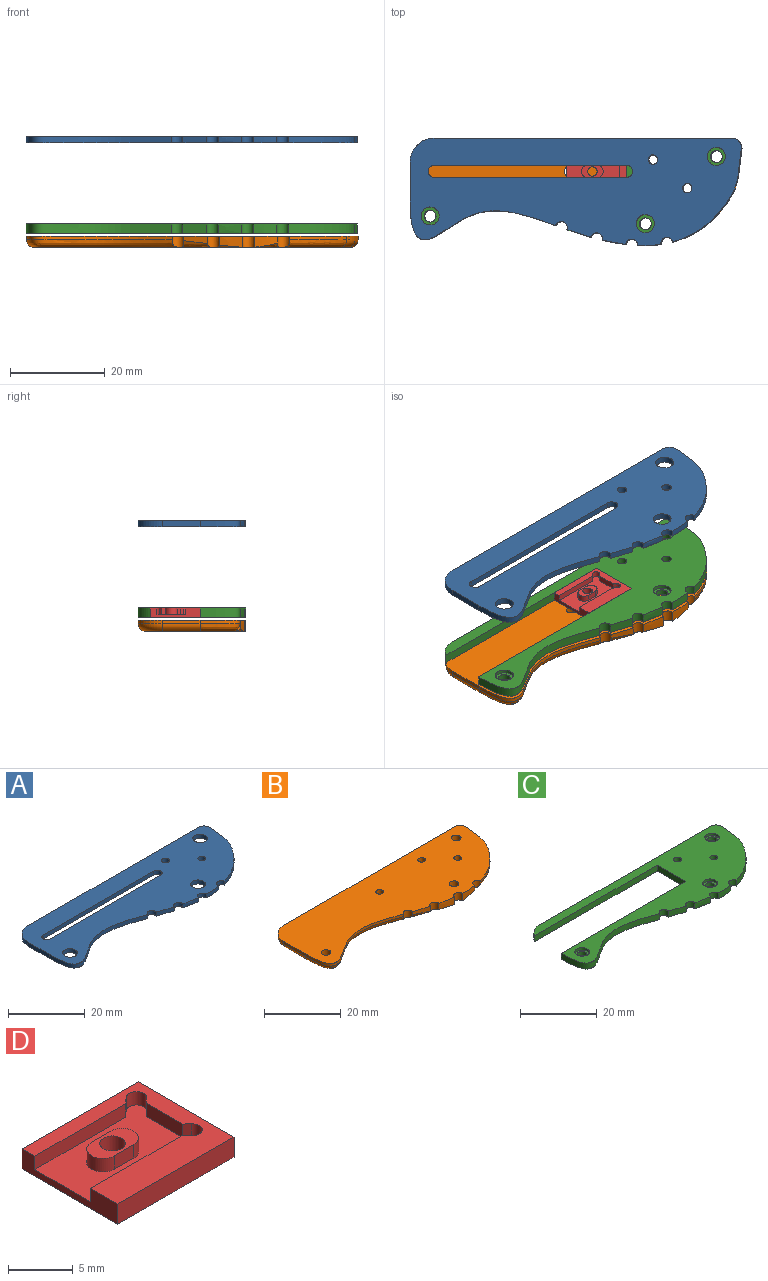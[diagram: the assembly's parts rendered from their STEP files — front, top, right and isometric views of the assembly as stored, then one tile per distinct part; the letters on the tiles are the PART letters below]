
ASSEMBLY  parts=4 mates=3
PART A: 26 faces, bbox 69.9x23.5x1.3 mm
  f0: plane 69.91x23.5mm, normal (0,0,-1), area 1147mm2, adj f2,f3,f4,f5,f6,f7,f8,f9
  f1: plane 69.91x23.5mm, normal (0,0,1), area 1147mm2, adj f2,f3,f4,f5,f6,f7,f8,f9
  f2: cylinder r=5.08mm len=5.08mm, axis (0,0,-1), area 10.1mm2, adj f0,f1,f3,f15
  f3: plane 62.8x1.27mm, normal (0,1,0), area 79.8mm2, adj f0,f1,f2,f4
  f4: cylinder r=2.03mm len=2.28mm, axis (0,0,-1), area 4.4mm2, adj f0,f1,f3,f5
  f5: plane 5.5x1.27mm, normal (0.99,-0.12,0), area 7mm2, adj f0,f1,f4,f6
  f6: cylinder r=11.43mm len=4.75mm, axis (0,0,-1), area 6.5mm2, adj f0,f1,f5,f7
  f7: extruded ~12.06x9.35mm, area 19.8mm2, adj f0,f1,f6,f8
  f8: cylinder r=1.27mm len=2.5mm, axis (0,0,-1), area 5mm2, adj f0,f1,f7,f9
  f9: extruded ~4.92x1.27mm, area 6.3mm2, adj f0,f1,f8,f10
  f10: cylinder r=1.27mm len=2.53mm, axis (0,0,-1), area 5mm2, adj f0,f1,f9,f11
  f11: extruded ~4.94x1.27mm, area 6.4mm2, adj f0,f1,f10,f12
  f12: cylinder r=1.27mm len=2.5mm, axis (0,0,-1), area 5mm2, adj f0,f1,f11,f13
  f13: extruded ~5.01x1.6mm, area 6.7mm2, adj f0,f1,f12,f14
  f14: cylinder r=1.27mm len=2.47mm, axis (0,0,-1), area 5.1mm2, adj f0,f1,f13,f16
  f15: plane 7.94x1.27mm, normal (-1,0,0), area 10.1mm2, adj f0,f1,f2,f16
  f16: extruded ~30.72x8.36mm, area 49.9mm2, adj f0,f1,f14,f15
  f17: cylinder r=1.27mm len=2.54mm, axis (0,0,1), area 5.1mm2, adj f0,f1,f18,f20
  f18: plane 40.64x1.27mm, normal (0,-1,0), area 51.6mm2, adj f0,f1,f17,f19
  f19: cylinder r=1.27mm len=2.54mm, axis (0,0,1), area 5.1mm2, adj f0,f1,f18,f20
  f20: plane 40.64x1.27mm, normal (0,1,0), area 51.6mm2, adj f0,f1,f17,f19
  f21: cylinder r=1mm len=2mm, axis (0,0,-1), area 8mm2, adj f0,f1
  f22: cylinder r=1mm len=2mm, axis (0,0,-1), area 8mm2, adj f0,f1
  f23: cylinder r=1.9mm len=3.8mm, axis (0,0,1), area 15.2mm2, adj f0,f1
  f24: cylinder r=1.9mm len=3.8mm, axis (0,0,1), area 15.2mm2, adj f0,f1
  f25: cylinder r=1.9mm len=3.8mm, axis (0,0,1), area 15.2mm2, adj f0,f1
PART B: 38 faces, bbox 71.2x31x2.4 mm
  f0: plane 66.74x20.69mm, normal (0,0,-1), area 899mm2, adj f11,f17,f18,f19,f20,f21,f22,f23
  f1: plane 69.91x23.5mm, normal (0,0,1), area 1271.4mm2, adj f2,f3,f4,f5,f6,f7,f8,f9
  f2: plane 7.94x0.79mm, normal (-1,0,0), area 6.3mm2, adj f1,f3,f16,f31
  f3: cylinder r=5.08mm len=5.08mm, axis (0,0,1), area 6.3mm2, adj f1,f2,f4,f32
  f4: plane 62.8x0.79mm, normal (0,1,0), area 49.8mm2, adj f1,f3,f5,f33
  f5: cylinder r=2.03mm len=2.28mm, axis (0,0,1), area 2.7mm2, adj f1,f4,f6,f34
  f6: plane 5.5x0.79mm, normal (0.99,-0.12,0), area 4.4mm2, adj f1,f5,f7,f35
  f7: cylinder r=11.43mm len=4.75mm, axis (0,0,1), area 4mm2, adj f1,f6,f8,f36
  f8: extruded ~12.06x9.35mm, area 12.4mm2, adj f1,f7,f9,f37
  f9: cylinder r=1.27mm len=2.5mm, axis (0,0,1), area 8.3mm2, adj f1,f8,f10,f37
  f10: extruded ~4.92x2.34mm, area 9.4mm2, adj f1,f9,f11,f37
  f11: cylinder r=1.27mm len=2.53mm, axis (0,0,1), area 9.4mm2, adj f0,f1,f10,f12,f30,f37
  f12: extruded ~4.94x2.34mm, area 10.6mm2, adj f1,f11,f13,f30
  f13: cylinder r=1.27mm len=2.5mm, axis (0,0,1), area 6.8mm2, adj f1,f12,f14,f30
  f14: extruded ~5.01x1.6mm, area 6.6mm2, adj f1,f13,f15,f30
  f15: cylinder r=1.27mm len=2.47mm, axis (0,0,1), area 8.3mm2, adj f1,f14,f16,f30
  f16: extruded ~30.72x8.36mm, area 31.2mm2, adj f1,f2,f15,f30
  f17: cylinder r=1.25mm len=2.5mm, axis (0,0,1), area 18.7mm2, adj f0,f1
  f18: cylinder r=1.25mm len=2.5mm, axis (0,0,1), area 18.7mm2, adj f0,f1
  f19: cylinder r=1.25mm len=2.5mm, axis (0,0,1), area 18.7mm2, adj f0,f1
  f20: cylinder r=1mm len=2.38mm, axis (0,0,1), area 15mm2, adj f0,f1
  f21: plane 11.32x0.79mm, normal (0,1,0), area 9mm2, adj f0,f22,f26,f27
  f22: cylinder r=1.27mm len=1.27mm, axis (0,0,-1), area 1.6mm2, adj f0,f21,f23,f27
  f23: plane 7.94x0.79mm, normal (1,0,0), area 6.3mm2, adj f0,f22,f24,f27
  f24: cylinder r=1.27mm len=1.27mm, axis (0,0,-1), area 1.6mm2, adj f0,f23,f25,f27
  f25: plane 11.32x0.79mm, normal (0,-1,0), area 9mm2, adj f0,f24,f26,f27
  f26: plane 10.48x0.79mm, normal (-1,0,0), area 8.3mm2, adj f0,f21,f25,f27
  f27: plane 12.59x10.48mm, normal (0,0,-1), area 124.9mm2, adj f21,f22,f23,f24,f25,f26,f28,f29
  f28: cylinder r=1mm len=2mm, axis (0,0,-1), area 10mm2, adj f1,f27
  f29: cylinder r=1mm len=2mm, axis (0,0,-1), area 10mm2, adj f1,f27
  f30: bspline ~65.23x24.38mm, area 114.3mm2, adj f0,f11,f12,f13,f14,f15,f16,f31
  f31: cylinder r=1.59mm len=7.94mm, axis (0,-1,0), area 19.8mm2, adj f0,f2,f30,f32
  f32: torus R=3.49mm, axis (0,0,-1), area 17.6mm2, adj f0,f3,f31,f33
  f33: cylinder r=1.59mm len=62.8mm, axis (-1,0,0), area 156.6mm2, adj f0,f4,f32,f34
  f34: torus R=0.45mm, axis (0,0,-1), area 6.2mm2, adj f0,f5,f33,f35
  f35: cylinder r=1.59mm len=5.69mm, axis (0.12,0.99,0), area 13.8mm2, adj f0,f6,f34,f36
  f36: torus R=9.84mm, axis (0,0,-1), area 12.1mm2, adj f0,f7,f35,f37
  f37: bspline ~30.16x19.22mm, area 44.5mm2, adj f0,f8,f9,f10,f11,f36
PART C: 30 faces, bbox 69.9x23.5x1.9 mm
  f0: cylinder r=1.25mm len=2.5mm, axis (0,0,1), area 9.2mm2, adj f21,f26
  f1: cylinder r=1.25mm len=2.5mm, axis (0,0,1), area 9.2mm2, adj f21,f24
  f2: cylinder r=1.25mm len=2.5mm, axis (0,0,1), area 9.2mm2, adj f21,f28
  f3: plane 69.91x23.5mm, normal (0,0,1), area 776.8mm2, adj f4,f5,f6,f7,f8,f9,f10,f11
  f4: plane 45.04x1.91mm, normal (0,-1,0), area 85.8mm2, adj f3,f5,f20,f21
  f5: plane 10.48x1.91mm, normal (-1,0,0), area 20mm2, adj f3,f4,f6,f21
  f6: plane 45.72x1.91mm, normal (0,1,0), area 87.1mm2, adj f3,f5,f7,f21
  f7: extruded ~30.72x8.36mm, area 74.8mm2, adj f3,f6,f8,f21
  f8: cylinder r=1.27mm len=2.47mm, axis (0,0,1), area 7.6mm2, adj f3,f7,f9,f21
  f9: extruded ~5.01x1.91mm, area 10mm2, adj f3,f8,f10,f21
  f10: cylinder r=1.27mm len=2.5mm, axis (0,0,1), area 7.5mm2, adj f3,f9,f11,f21
  f11: extruded ~4.94x1.91mm, area 9.6mm2, adj f3,f10,f12,f21
  f12: cylinder r=1.27mm len=2.53mm, axis (0,0,1), area 7.5mm2, adj f3,f11,f13,f21
  f13: extruded ~4.92x1.91mm, area 9.4mm2, adj f3,f12,f14,f21
  f14: cylinder r=1.27mm len=2.5mm, axis (0,0,1), area 7.5mm2, adj f3,f13,f15,f21
  f15: extruded ~12.06x9.35mm, area 29.8mm2, adj f3,f14,f16,f21
  f16: cylinder r=11.43mm len=4.75mm, axis (0,0,1), area 9.7mm2, adj f3,f15,f17,f21
  f17: plane 5.5x1.91mm, normal (0.99,-0.12,0), area 10.5mm2, adj f3,f16,f18,f21
  f18: cylinder r=2.03mm len=2.28mm, axis (0,0,1), area 6.6mm2, adj f3,f17,f19,f21
  f19: plane 62.8x1.91mm, normal (0,1,0), area 119.6mm2, adj f3,f18,f20,f21
  f20: cylinder r=5.08mm len=4.4mm, axis (0,0,1), area 10.1mm2, adj f3,f4,f19,f21
  f21: plane 69.91x23.5mm, normal (0,0,-1), area 796.1mm2, adj f0,f1,f2,f4,f5,f6,f7,f8
  f22: cylinder r=1mm len=2mm, axis (0,0,-1), area 12mm2, adj f3,f21
  f23: cylinder r=1mm len=2mm, axis (0,0,-1), area 12mm2, adj f3,f21
  f24: plane 3.8x3.8mm, normal (0,0,1), area 6.4mm2, adj f1,f25
  f25: cylinder r=1.9mm len=3.8mm, axis (0,0,1), area 8.7mm2, adj f3,f24
  f26: plane 3.8x3.8mm, normal (0,0,1), area 6.4mm2, adj f0,f27
  f27: cylinder r=1.9mm len=3.8mm, axis (0,0,1), area 8.7mm2, adj f3,f26
  f28: plane 3.8x3.8mm, normal (0,0,1), area 6.4mm2, adj f2,f29
  f29: cylinder r=1.9mm len=3.8mm, axis (0,0,1), area 8.7mm2, adj f3,f28
PART D: 24 faces, bbox 12.7x10.5x1.9 mm
  f0: plane 3.98x1.27mm, normal (-1,0,0), area 5.1mm2, adj f1,f2,f16,f21
  f1: plane 12.7x10.48mm, normal (0,0,1), area 62.1mm2, adj f0,f3,f4,f5,f6,f7,f14,f15
  f2: plane 11.91x7.68mm, normal (0,0,1), area 60.6mm2, adj f0,f5,f6,f7,f8,f9,f12,f13
  f3: plane 10.48x1.91mm, normal (1,0,0), area 20mm2, adj f1,f4,f22,f23
  f4: plane 12.7x1.91mm, normal (0,1,0), area 24.2mm2, adj f1,f3,f5,f23
  f5: plane 10.48x1.91mm, normal (-1,0,0), area 12.2mm2, adj f1,f2,f4,f6,f7,f22,f23
  f6: plane 9.92x1.27mm, normal (0,-1,0), area 12.6mm2, adj f1,f2,f5,f15
  f7: plane 9.92x1.27mm, normal (0,1,0), area 12.6mm2, adj f1,f2,f5,f18
  f8: plane 2.1x1.27mm, normal (0,-1,0), area 2.7mm2, adj f2,f9,f10,f12
  f9: cylinder r=1.27mm len=2.54mm, axis (0,0,1), area 5.1mm2, adj f2,f8,f10,f13
  f10: plane 4.64x2.54mm, normal (0,0,1), area 7.2mm2, adj f8,f9,f11,f12,f13
  f11: cylinder r=1mm len=2mm, axis (0,0,1), area 12mm2, adj f10,f23
  f12: cylinder r=1.27mm len=2.54mm, axis (0,0,1), area 5.1mm2, adj f2,f8,f10,f13
  f13: plane 2.1x1.27mm, normal (0,1,0), area 2.7mm2, adj f2,f9,f10,f12
  f14: plane 1.27x0.6mm, normal (0.66,-0.75,0), area 1mm2, adj f1,f2,f15,f17
  f15: cylinder r=0.79mm len=1.27mm, axis (0,0,1), area 0.1mm2, adj f1,f2,f6,f14
  f16: plane 1.27x0.52mm, normal (-0.66,0.75,0), area 0.9mm2, adj f0,f1,f2,f17
  f17: cylinder r=0.79mm len=1.39mm, axis (0,0,1), area 3.2mm2, adj f1,f2,f14,f16
  f18: cylinder r=0.79mm len=1.27mm, axis (0,0,1), area 0.1mm2, adj f1,f2,f7,f19
  f19: plane 1.27x0.6mm, normal (0.66,0.75,0), area 1mm2, adj f1,f2,f18,f20
  f20: cylinder r=0.79mm len=1.39mm, axis (0,0,1), area 3.2mm2, adj f1,f2,f19,f21
  f21: plane 1.27x0.52mm, normal (-0.66,-0.75,0), area 0.9mm2, adj f0,f1,f2,f20
  f22: plane 12.7x1.91mm, normal (0,-1,0), area 24.2mm2, adj f1,f3,f5,f23
  f23: plane 12.7x10.48mm, normal (0,0,-1), area 129.9mm2, adj f3,f4,f5,f11,f22
PLACE A t=(-4.03,2.83,16.82)mm
PLACE B t=(-3.88,2.83,-1.02)mm
PLACE C t=(-4.03,2.83,-0.36)mm fixed
PLACE D t=(1.05,2.83,-0.36)mm
MATE slider D.f3 <-> C.f5  axis (1,0,0) through (7.4,2.04,0.91)mm
MATE planar A.f5 <-> C.f17  axis (0.99,-0.12,0) through (31.24,4.79,18.73)mm
MATE planar C.f19 <-> B.f4  axis (0,1,0) through (-1.84,9.82,-0.04)mm
